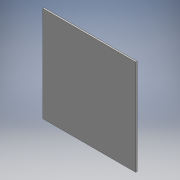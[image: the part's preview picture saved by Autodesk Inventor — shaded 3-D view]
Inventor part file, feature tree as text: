
AUTODESK INVENTOR PART (.ipt)
format: ipt  version: 2016 (Build 200138000, 138)  size: 85,504 bytes
history: native  units: mm
features: other x1, extrude x1, sketch x1
ambient origin geometry x8: Origin, YZ Plane, XZ Plane, XY Plane, X Axis, Y Axis, Z Axis, Center Point
bodies: Body1 (feature_tree)
feature tree (3):
  other  "ソリッド1"
  extrude  "押し出し1"  Depth=136.0mm
  sketch  "スケッチ1"
